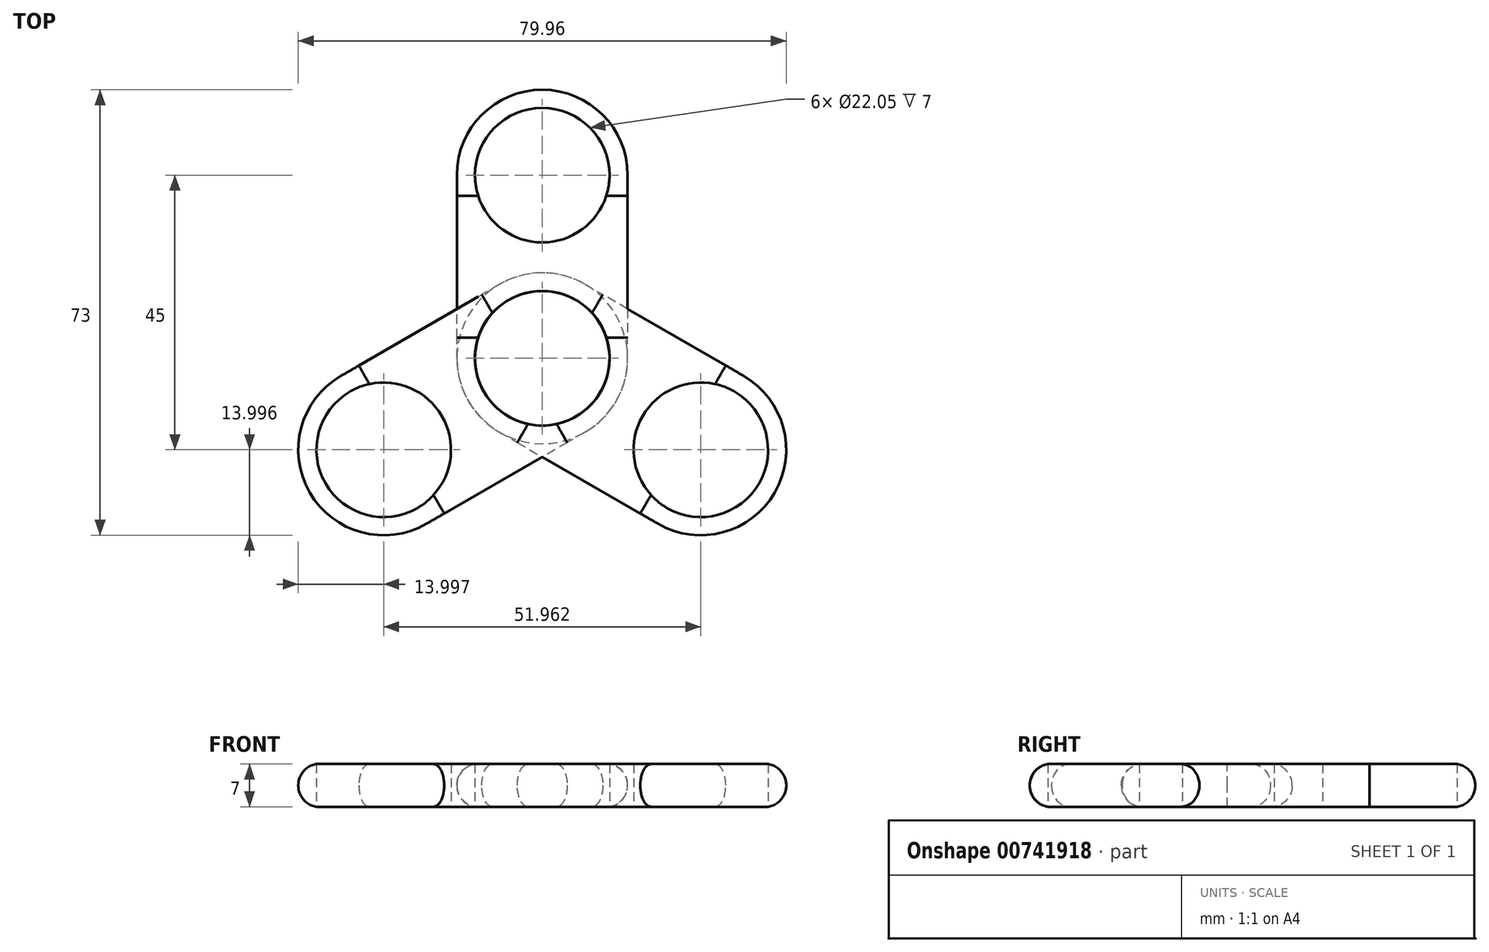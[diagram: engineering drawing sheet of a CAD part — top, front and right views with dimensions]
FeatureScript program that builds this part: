
annotation { "Feature Type Name" : "Feature", "Feature Type Description" : "" }
export const myFeature = defineFeature(function(context is Context, id is Id, definition is map)
    precondition{}
    {
        {
            var Q0;
            Q0=qCreatedBy(makeId("Top.planeOp"),FACE);
            var sketch = newSketch(context, id + "F0", { "sketchPlane" : qUnion([Q0])});
            skLineSegment(sketch, "E0.bottom", {"start": v(16.86, -27.43) * mm, "end": v(-11.14, -27.43) * mm});
            skLineSegment(sketch, "E0.top", {"start": v(16.86, 2.57) * mm, "end": v(-11.14, 2.57) * mm});
            skLineSegment(sketch, "E0.left", {"start": v(16.86, -27.43) * mm, "end": v(16.86, 2.57) * mm});
            skLineSegment(sketch, "E0.right", {"start": v(-11.14, -27.43) * mm, "end": v(-11.14, 2.57) * mm});
            skCircle(sketch, "E1", {"center": v(2.86, -27.43) * mm, "radius": 14 * mm});
            skCircle(sketch, "E2", {"center": v(2.86, -27.43) * mm, "radius": 11.03 * mm});
            skCircle(sketch, "E3", {"center": v(2.86, 2.57) * mm, "radius": 14 * mm});
            skCircle(sketch, "E4", {"center": v(2.86, 2.57) * mm, "radius": 11.03 * mm});
            skSolve(sketch);
        }
        {
            var Q0;
            {var subQ0=sQuery(id+"F0.wireOp",EDGE,"E0.left");Q0=makeQuery(id+"F0.imprint","IMPRINT",FACE,{"disambiguationData":[TD([[makeQuery(id+"F0.imprint","IMPRINT",EDGE,{"derivedFrom":subQ0}),1.0]])]});}
            var Q1;
            {var subQ1=sQuery(id+"F0.wireOp",EDGE,"E0.top");var subQ3=sQuery(id+"F0.wireOp",EDGE,"E4");var subQ4=makeQuery(id+"F0.imprint","INTERSECT",VERTEX,{"disambiguationData":[OD(0.0)],"derivedFrom":[subQ1,subQ3]});Q1=makeQuery(id+"F0.imprint","IMPRINT",FACE,{"disambiguationData":[TD([[makeQuery(id+"F0.imprint","IMPRINT",EDGE,{"disambiguationData":[TD([[subQ4,-1.0]])],"derivedFrom":subQ3}),-1.0]])]});}
            var Q2;
            {var subQ1=sQuery(id+"F0.wireOp",EDGE,"E0.top");var subQ3=sQuery(id+"F0.wireOp",EDGE,"E4");var subQ4=makeQuery(id+"F0.imprint","INTERSECT",VERTEX,{"disambiguationData":[OD(0.0)],"derivedFrom":[subQ1,subQ3]});Q2=makeQuery(id+"F0.imprint","IMPRINT",FACE,{"disambiguationData":[TD([[makeQuery(id+"F0.imprint","IMPRINT",EDGE,{"disambiguationData":[TD([[subQ4,1.0]])],"derivedFrom":subQ3}),-1.0]])]});}
            var Q3;
            {var subQ1=sQuery(id+"F0.wireOp",EDGE,"E0.bottom");var subQ3=sQuery(id+"F0.wireOp",EDGE,"E2");var subQ4=makeQuery(id+"F0.imprint","INTERSECT",VERTEX,{"disambiguationData":[OD(0.0)],"derivedFrom":[subQ1,subQ3]});Q3=makeQuery(id+"F0.imprint","IMPRINT",FACE,{"disambiguationData":[TD([[makeQuery(id+"F0.imprint","IMPRINT",EDGE,{"disambiguationData":[TD([[subQ4,-1.0]])],"derivedFrom":subQ3}),-1.0]])]});}
            var Q4;
            {var subQ1=sQuery(id+"F0.wireOp",EDGE,"E0.bottom");var subQ3=sQuery(id+"F0.wireOp",EDGE,"E2");var subQ4=makeQuery(id+"F0.imprint","INTERSECT",VERTEX,{"disambiguationData":[OD(0.0)],"derivedFrom":[subQ1,subQ3]});Q4=makeQuery(id+"F0.imprint","IMPRINT",FACE,{"disambiguationData":[TD([[makeQuery(id+"F0.imprint","IMPRINT",EDGE,{"disambiguationData":[TD([[subQ4,1.0]])],"derivedFrom":subQ3}),-1.0]])]});}
            extrude(context, id + "F1", {"entities" : qUnion([Q0, Q1, Q2, Q3, Q4]), "depth" : 7 * mm, "offsetDistance" : 25.4 * mm});
        }
        {
            var Q0;
            Q0=makeQuery(id+"F1.opExtrude","SWEPT_BODY",BODY,{"disambiguationData":[OSD([sQuery(id+"F0.wireOp",EDGE,"E0.left"),sQuery(id+"F0.wireOp",EDGE,"E0.right"),sQuery(id+"F0.wireOp",EDGE,"E1"),sQuery(id+"F0.wireOp",EDGE,"E2"),sQuery(id+"F0.wireOp",EDGE,"E3"),sQuery(id+"F0.wireOp",EDGE,"E4")])]});
            var Q1;
            Q1=makeQuery(id+"F1.opExtrude","SWEPT_FACE",FACE,{"disambiguationData":[OSD([sQuery(id+"F0.wireOp",EDGE,"E1")])]});
            circularPattern(context, id + "F2", {"entities" : qUnion([Q0]), "axis" : qUnion([Q1]), "angle" : 360 * degree, "instanceCount" : 3, "equalSpace" : true});
        }
        {
            var Q0;
            Q0=makeQuery(id+"F2.opPattern","COPY",EDGE,{"derivedFrom":makeQuery(id+"F1.opExtrude","CAP_EDGE",EDGE,{"disambiguationData":[OSD([sQuery(id+"F0.wireOp",EDGE,"E3")])],"isStart":true}),"instanceName":"1"});
            var Q1;
            Q1=makeQuery(id+"F2.opPattern","COPY",EDGE,{"derivedFrom":makeQuery(id+"F1.opExtrude","CAP_EDGE",EDGE,{"disambiguationData":[OSD([sQuery(id+"F0.wireOp",EDGE,"E3")])],"isStart":false}),"instanceName":"1"});
            var Q2;
            Q2=makeQuery(id+"F1.opExtrude","CAP_EDGE",EDGE,{"disambiguationData":[OSD([sQuery(id+"F0.wireOp",EDGE,"E0.left")])],"isStart":false});
            var Q3;
            Q3=makeQuery(id+"F2.opPattern","COPY",EDGE,{"derivedFrom":makeQuery(id+"F1.opExtrude","CAP_EDGE",EDGE,{"disambiguationData":[OSD([sQuery(id+"F0.wireOp",EDGE,"E0.right")])],"isStart":false}),"instanceName":"1"});
            var Q4;
            Q4=makeQuery(id+"F2.opPattern","COPY",EDGE,{"derivedFrom":makeQuery(id+"F1.opExtrude","CAP_EDGE",EDGE,{"disambiguationData":[OSD([sQuery(id+"F0.wireOp",EDGE,"E0.left")])],"isStart":false}),"instanceName":"1"});
            var Q5;
            Q5=makeQuery(id+"F2.opPattern","COPY",EDGE,{"derivedFrom":makeQuery(id+"F1.opExtrude","CAP_EDGE",EDGE,{"disambiguationData":[OSD([sQuery(id+"F0.wireOp",EDGE,"E0.left")])],"isStart":true}),"instanceName":"1"});
            var Q6;
            Q6=makeQuery(id+"F2.opPattern","COPY",EDGE,{"derivedFrom":makeQuery(id+"F1.opExtrude","CAP_EDGE",EDGE,{"disambiguationData":[OSD([sQuery(id+"F0.wireOp",EDGE,"E0.right")])],"isStart":false}),"instanceName":"2"});
            var Q7;
            Q7=makeQuery(id+"F2.opPattern","COPY",EDGE,{"derivedFrom":makeQuery(id+"F1.opExtrude","CAP_EDGE",EDGE,{"disambiguationData":[OSD([sQuery(id+"F0.wireOp",EDGE,"E0.right")])],"isStart":true}),"instanceName":"2"});
            var Q8;
            Q8=makeQuery(id+"F2.opPattern","COPY",EDGE,{"derivedFrom":makeQuery(id+"F1.opExtrude","CAP_EDGE",EDGE,{"disambiguationData":[OSD([sQuery(id+"F0.wireOp",EDGE,"E3")])],"isStart":true}),"instanceName":"2"});
            var Q9;
            Q9=makeQuery(id+"F2.opPattern","COPY",EDGE,{"derivedFrom":makeQuery(id+"F1.opExtrude","CAP_EDGE",EDGE,{"disambiguationData":[OSD([sQuery(id+"F0.wireOp",EDGE,"E3")])],"isStart":false}),"instanceName":"2"});
            var Q10;
            Q10=makeQuery(id+"F1.opExtrude","CAP_EDGE",EDGE,{"disambiguationData":[OSD([sQuery(id+"F0.wireOp",EDGE,"E0.left")])],"isStart":true});
            var Q11;
            Q11=makeQuery(id+"F1.opExtrude","CAP_EDGE",EDGE,{"disambiguationData":[OSD([sQuery(id+"F0.wireOp",EDGE,"E3")])],"isStart":true});
            fillet(context, id + "F3", {"entities" : qUnion([Q0, Q1, Q2, Q3, Q4, Q5, Q6, Q7, Q8, Q9, Q10, Q11]), "radius" : 3.5 * mm, "tangentPropagation" : true, "allowEdgeOverflow" : false});
        }
    });
